# Revit family: FAPSUB-1
name_source: partatom
category: Communication Devices
revit_build: Autodesk Revit 2014 (Build: 20140709_2115(x64)
units: mm (PartAtom-declared; Revit-internal decimal feet)

## types (1)
- Two Way, Full Range, Coaxial Ceiling Loudspeaker
    100V Taps = 1.9, 3.8, 7.5, 15, 30, 60 Watts & 8Ω
    70V Taps = 1.9, 3.8, 7.5, 15, 30, 60 Watts & 8Ω
    Baffle Material = <By Category>
    Body Material = QF_Plastic - White - Smooth
    Color = <By Category>
    Controls = Front Mounted Tap Selector Switch.
    Cost = 267.99 $
    Cost MSRP = 267.99 $
    Coverage Horizontal = 110.00°
    Coverage Vertical = 110.00°
    Description = 8" TUNED PORTED IN-CEILING SUBWOOFER WITH 60-WATT 70V/100V TRANSFORMER
    Dispersion Angle = 90.00°
    Enclosure Material = <By Category>
    Family Code (default) = LOUD SPEAKERS
    Frequency Response  = 45Hz – 120Hz (±10dB),55Hz – 100Hz (±6dB)
    Grill Material = QF_Plastic - Black - Fine Textured
    Height = 12.75 "
    IQ Category = SPEAKERS
    Impedance = 8
    Ingress Protection = IP-21
    Input Connectors = 4 Pole Detachable Phoenix / Euro Style Connector Allows Easy Pre-Wiring
    Manufacturer = ATLAS SOUND
    Manufacturer URL = https://www.atlasied.com
    MasterFormat = 27 41 13
    MaterFormat Title = SPEAKERS
    Model = FABSUB-1
    Mount Material = QF_Plastic - White - Smooth
    OmniClass Number = 23-37 17 13 19
    OmniClass Title = SPEAKERS
    Power Handling = 100
    Power Rating (RMS) = 100 Watts
    Product Documentation Link = https://www.atlasied.com
    Product Page URL = https://www.atlasied.com
    Regulatory Compliance = UL Listed to Comply with UL1480
    SPL Max = 107
    Safety Agency Ratings = UL Listed to Comply with UL1480
    ScheduleType |RF| = AtlasIED Master
    Sensitivity = 89
    Speaker Dispersion = 120.00°
    Speaker Type = S1
    Transformer Option = Yes
    URL = www.atlassound.com
    Vertical Symmetry = Yes
    Warranty = 5 Year
    Width = 15.75 "

## geometry (parser evidence)
native form markers: Blend x6, Sweep x2
no freeform markers — native parametric forms only
